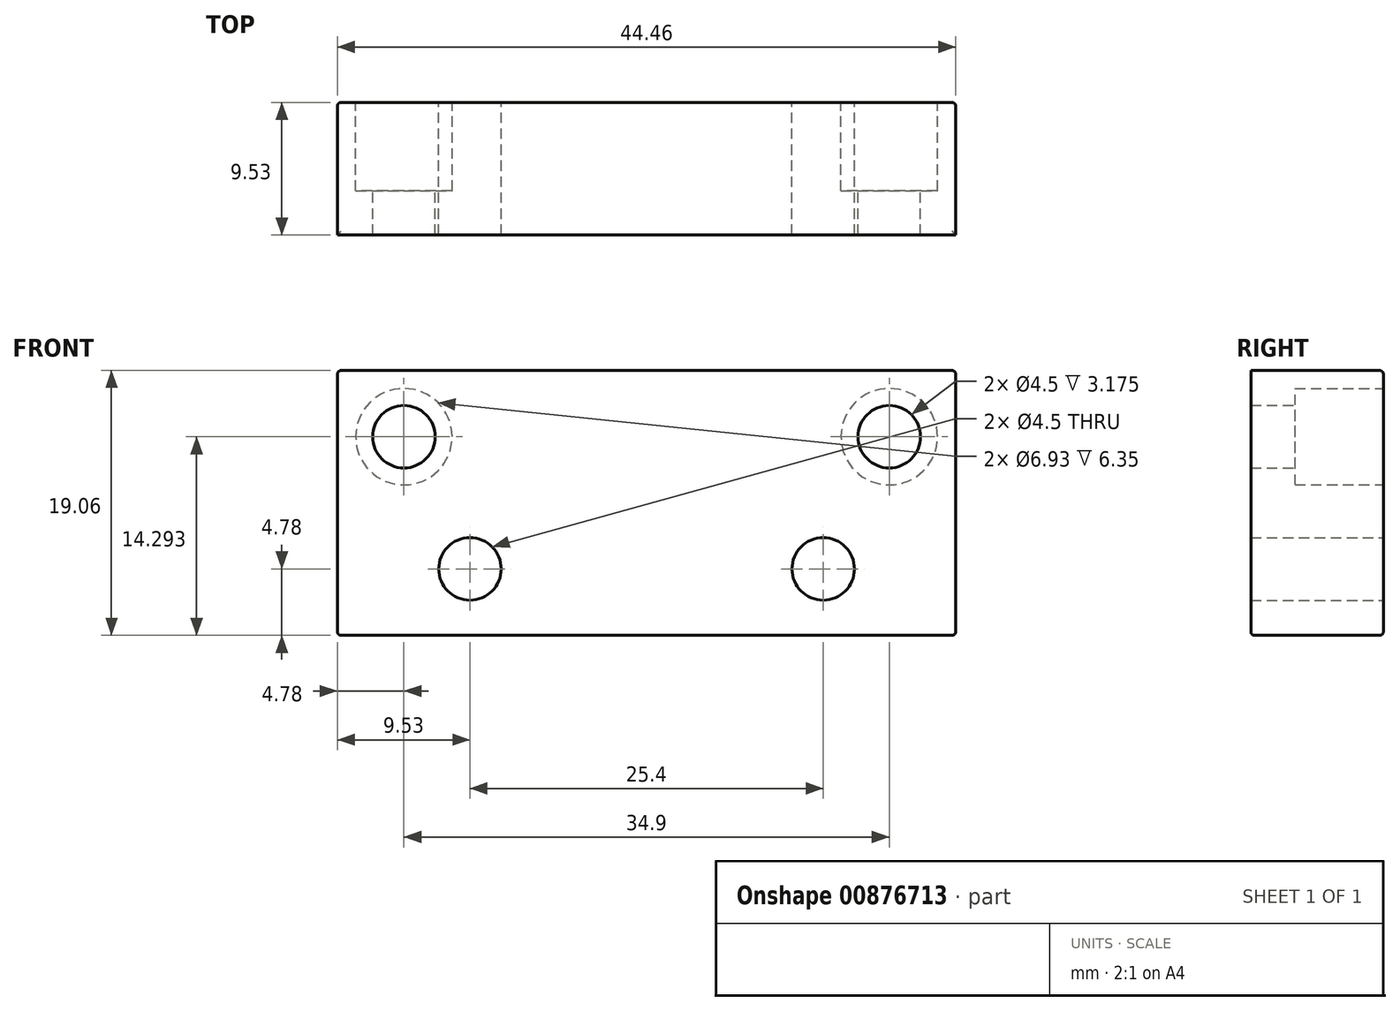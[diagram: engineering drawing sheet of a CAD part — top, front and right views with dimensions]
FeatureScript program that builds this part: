
annotation { "Feature Type Name" : "Feature", "Feature Type Description" : "" }
export const myFeature = defineFeature(function(context is Context, id is Id, definition is map)
    precondition{}
    {
        {
            var Q0;
            Q0=qCreatedBy(makeId("Front.planeOp"),FACE);
            var sketch = newSketch(context, id + "F0", { "sketchPlane" : qUnion([Q0])});
            skLineSegment(sketch, "E0.bottom", {"start": v(22.23, 9.53) * mm, "end": v(-22.23, 9.53) * mm});
            skLineSegment(sketch, "E0.top", {"start": v(22.23, -9.53) * mm, "end": v(-22.23, -9.53) * mm});
            skLineSegment(sketch, "E0.left", {"start": v(22.23, 9.53) * mm, "end": v(22.23, -9.53) * mm});
            skLineSegment(sketch, "E0.right", {"start": v(-22.23, 9.53) * mm, "end": v(-22.23, -9.53) * mm});
            skPoint(sketch, "E0.middle", {"position": v(0, 0) * mm});
            skPoint(sketch, "E1", {"position": v(17.45, 4.76) * mm});
            skPoint(sketch, "E2", {"position": v(-17.45, 4.76) * mm});
            skCircle(sketch, "E3", {"center": v(17.45, 4.76) * mm, "radius": 2.25 * mm});
            skCircle(sketch, "E4", {"center": v(-17.45, 4.76) * mm, "radius": 2.25 * mm});
            skPoint(sketch, "E5", {"position": v(-12.7, -4.75) * mm});
            skPoint(sketch, "E6", {"position": v(12.7, -4.75) * mm});
            skCircle(sketch, "E7", {"center": v(-12.7, -4.75) * mm, "radius": 2.25 * mm});
            skCircle(sketch, "E8", {"center": v(12.7, -4.75) * mm, "radius": 2.25 * mm});
            skCircle(sketch, "E9", {"center": v(-17.45, 4.76) * mm, "radius": 3.47 * mm});
            skCircle(sketch, "E10", {"center": v(17.45, 4.76) * mm, "radius": 3.47 * mm});
            skSolve(sketch);
        }
        {
            var Q0;
            Q0 = qSketchRegion(id + "F0", true);
            var Q1;
            Q1=makeQuery(id+"F0.imprint","IMPRINT",FACE,{"disambiguationData":[TD([[makeQuery(id+"F0.imprint","IMPRINT",EDGE,{"derivedFrom":sQuery(id+"F0.wireOp",EDGE,"E3")}),-1.0]])]});
            var Q2;
            Q2=makeQuery(id+"F0.imprint","IMPRINT",FACE,{"disambiguationData":[TD([[makeQuery(id+"F0.imprint","IMPRINT",EDGE,{"derivedFrom":sQuery(id+"F0.wireOp",EDGE,"E4")}),-1.0]])]});
            extrude(context, id + "F1", {"entities" : qUnion([Q0, Q1, Q2]), "depth" : 9.52 * mm, "offsetDistance" : 25.4 * mm});
        }
        {
            var Q0;
            Q0=makeQuery(id+"F0.imprint","IMPRINT",FACE,{"disambiguationData":[TD([[makeQuery(id+"F0.imprint","IMPRINT",EDGE,{"derivedFrom":sQuery(id+"F0.wireOp",EDGE,"E3")}),-1.0]])]});
            var Q1;
            Q1=makeQuery(id+"F0.imprint","IMPRINT",FACE,{"disambiguationData":[TD([[makeQuery(id+"F0.imprint","IMPRINT",EDGE,{"derivedFrom":sQuery(id+"F0.wireOp",EDGE,"E4")}),-1.0]])]});
            extrude(context, id + "F2", {"entities" : qUnion([Q0, Q1]), "operationType" : NewBodyOperationType.REMOVE, "depth" : 6.35 * mm, "offsetDistance" : 25.4 * mm});
        }
        {
            var Q0;
            Q0=makeQuery(id+"F1.opExtrude","SWEPT_EDGE",EDGE,{"disambiguationData":[OSD([sQuery(id+"F0.wireOp",EDGE,"E0.bottom"),sQuery(id+"F0.wireOp",EDGE,"E0.right")])]});
            var Q1;
            Q1=makeQuery(id+"F1.opExtrude","SWEPT_EDGE",EDGE,{"disambiguationData":[OSD([sQuery(id+"F0.wireOp",EDGE,"E0.top"),sQuery(id+"F0.wireOp",EDGE,"E0.right")])]});
            var Q2;
            Q2=makeQuery(id+"F1.opExtrude","SWEPT_EDGE",EDGE,{"disambiguationData":[OSD([sQuery(id+"F0.wireOp",EDGE,"E0.top"),sQuery(id+"F0.wireOp",EDGE,"E0.left")])]});
            var Q3;
            Q3=makeQuery(id+"F1.opExtrude","SWEPT_EDGE",EDGE,{"disambiguationData":[OSD([sQuery(id+"F0.wireOp",EDGE,"E0.bottom"),sQuery(id+"F0.wireOp",EDGE,"E0.left")])]});
            var Q4;
            Q4=makeQuery(id+"F1.opExtrude","CAP_EDGE",EDGE,{"disambiguationData":[OSD([sQuery(id+"F0.wireOp",EDGE,"E0.bottom")])],"isStart":true});
            var Q5;
            Q5=makeQuery(id+"F1.opExtrude","CAP_EDGE",EDGE,{"disambiguationData":[OSD([sQuery(id+"F0.wireOp",EDGE,"E0.right")])],"isStart":true});
            var Q6;
            Q6=makeQuery(id+"F1.opExtrude","CAP_EDGE",EDGE,{"disambiguationData":[OSD([sQuery(id+"F0.wireOp",EDGE,"E0.top")])],"isStart":true});
            var Q7;
            Q7=makeQuery(id+"F1.opExtrude","CAP_EDGE",EDGE,{"disambiguationData":[OSD([sQuery(id+"F0.wireOp",EDGE,"E0.left")])],"isStart":true});
            var Q8;
            Q8=makeQuery(id+"F1.opExtrude","CAP_EDGE",EDGE,{"disambiguationData":[OSD([sQuery(id+"F0.wireOp",EDGE,"E0.top")])],"isStart":false});
            fillet(context, id + "F3", {"entities" : qUnion([Q0, Q1, Q2, Q3, Q4, Q5, Q6, Q7, Q8]), "radius" : 0.25 * mm, "tangentPropagation" : true, "allowEdgeOverflow" : false});
        }
    });
